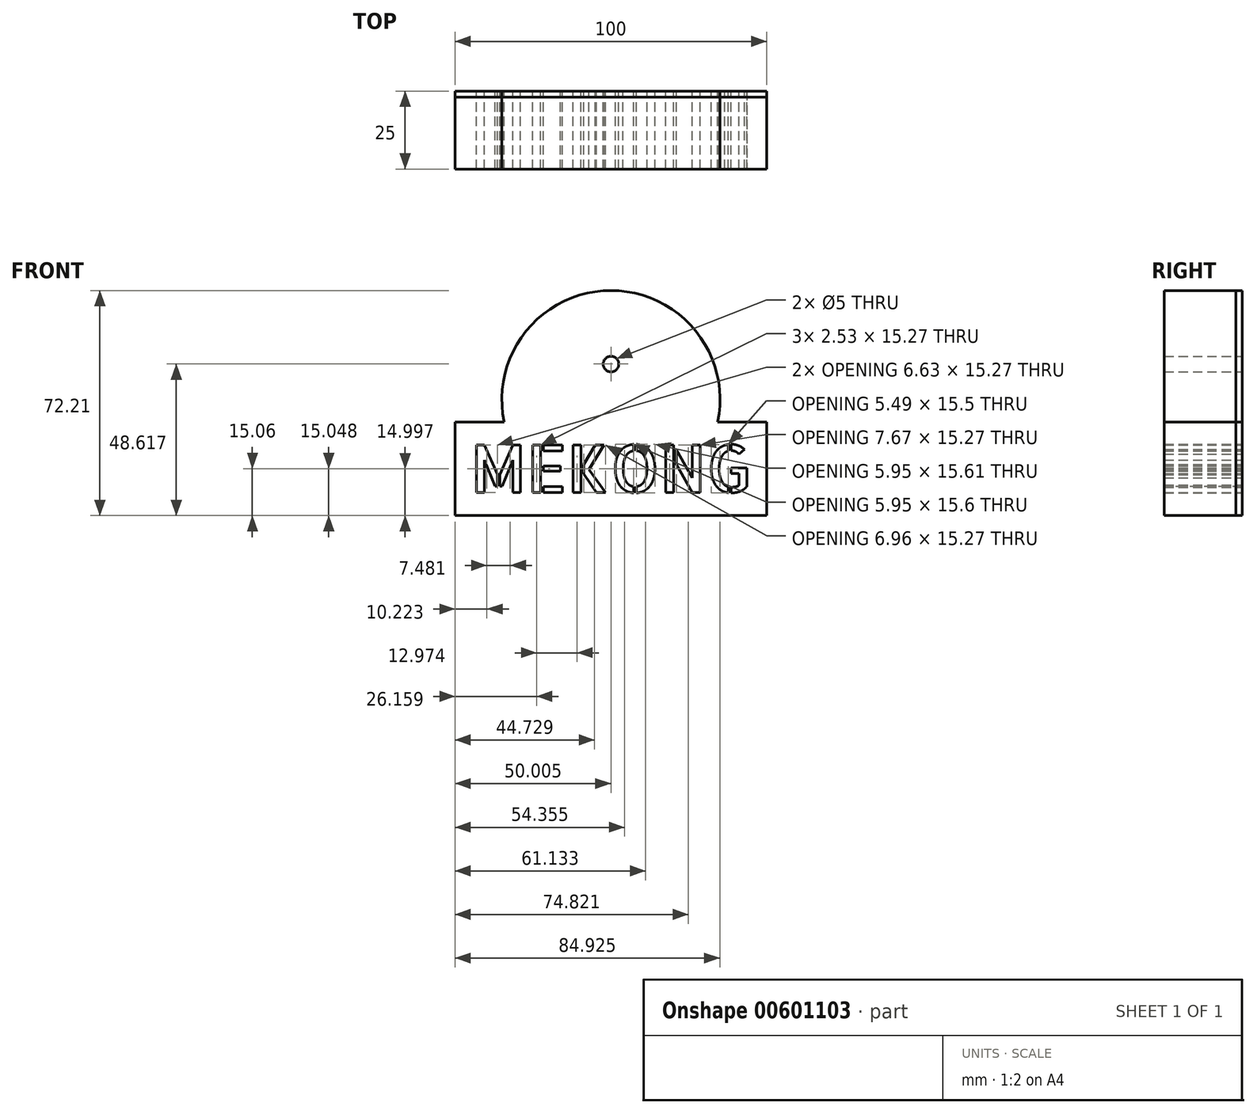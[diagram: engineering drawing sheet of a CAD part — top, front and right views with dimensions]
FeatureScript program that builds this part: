
annotation { "Feature Type Name" : "Feature", "Feature Type Description" : "" }
export const myFeature = defineFeature(function(context is Context, id is Id, definition is map)
    precondition{}
    {
        {
            var Q0;
            Q0=qCreatedBy(makeId("Front.planeOp"),FACE);
            var sketch = newSketch(context, id + "F0", { "sketchPlane" : qUnion([Q0])});
            skLineSegment(sketch, "E0.bottom", {"start": v(-209.66, -19.26) * mm, "end": v(-109.66, -19.26) * mm});
            skLineSegment(sketch, "E0.top", {"start": v(-209.66, 10.74) * mm, "end": v(-193.9, 10.74) * mm});
            skLineSegment(sketch, "E0.left", {"start": v(-209.66, -19.26) * mm, "end": v(-209.66, 10.74) * mm});
            skLineSegment(sketch, "E0.right", {"start": v(-109.66, -19.26) * mm, "end": v(-109.66, 10.74) * mm});
            skArc(sketch, "E1", {"start": v(-125.4, 10.74) * mm, "mid": v(-159.66, 52.95) * mm, "end": v(-193.9, 10.74) * mm});
            skCircle(sketch, "E2", {"center": v(-159.66, 29.36) * mm, "radius": 2.5 * mm});
            skPoint(sketch, "E3", {"position": v(-159.66, -19.26) * mm});
            skPoint(sketch, "E4", {"position": v(-109.66, -19.26) * mm});
            skPoint(sketch, "E5", {"position": v(-109.66, -4.26) * mm});
            skPoint(sketch, "E6", {"position": v(-109.66, 10.74) * mm});
            skText(sketch, "E7", { "text": "MEKONG", "fontName": "AllertaStencil-Regular.ttf"});
            skPoint(sketch, "E8", {"position": v(-159.66, -11.9) * mm});
            skPoint(sketch, "E9", {"position": v(-114.66, 3.38) * mm});
            skPoint(sketch, "E10", {"position": v(-114.66, -4.26) * mm});
            skLineSegment(sketch, "E11.trimOffspring", {"start": v(-125.4, 10.74) * mm, "end": v(-109.66, 10.74) * mm});
            const initialGuessF0  = {"E7": [-0.20466, -0.0119, 1, 0, 0.01528]};
            skSetInitialGuess(sketch, initialGuessF0);
            skSolve(sketch);
        }
        {
            var Q0;
            Q0 = qSketchRegion(id + "F0", true);
            var Q1;
            Q1=makeQuery(id+"F0.imprint","IMPRINT",FACE,{"disambiguationData":[TD([[makeQuery(id+"F0.imprint","IMPRINT",EDGE,{"derivedFrom":sQuery(id+"F0.wireOp",EDGE,"E0.bottom")}),1.0]])]});
            var Q2;
            Q2=makeQuery(id+"F0.imprint","IMPRINT",FACE,{"disambiguationData":[TD([[makeQuery(id+"F0.imprint","IMPRINT",EDGE,{"derivedFrom":sQuery(id+"F0.wireOp",EDGE,"E7.sketch_text.stroke-116")}),-1.0]])]});
            var Q3;
            Q3=makeQuery(id+"F0.imprint","IMPRINT",FACE,{"disambiguationData":[TD([[makeQuery(id+"F0.imprint","IMPRINT",EDGE,{"derivedFrom":sQuery(id+"F0.wireOp",EDGE,"E7.sketch_text.stroke-90")}),-1.0]])]});
            var Q4;
            Q4=makeQuery(id+"F0.imprint","IMPRINT",FACE,{"disambiguationData":[TD([[makeQuery(id+"F0.imprint","IMPRINT",EDGE,{"derivedFrom":sQuery(id+"F0.wireOp",EDGE,"E7.sketch_text.stroke-98")}),-1.0]])]});
            var Q5;
            Q5=makeQuery(id+"F0.imprint","IMPRINT",FACE,{"disambiguationData":[TD([[makeQuery(id+"F0.imprint","IMPRINT",EDGE,{"derivedFrom":sQuery(id+"F0.wireOp",EDGE,"E7.sketch_text.stroke-0")}),-1.0]])]});
            var Q6;
            Q6=makeQuery(id+"F0.imprint","IMPRINT",FACE,{"disambiguationData":[TD([[makeQuery(id+"F0.imprint","IMPRINT",EDGE,{"derivedFrom":sQuery(id+"F0.wireOp",EDGE,"E7.sketch_text.stroke-8")}),-1.0]])]});
            var Q7;
            Q7=makeQuery(id+"F0.imprint","IMPRINT",FACE,{"disambiguationData":[TD([[makeQuery(id+"F0.imprint","IMPRINT",EDGE,{"derivedFrom":sQuery(id+"F0.wireOp",EDGE,"E7.sketch_text.stroke-16")}),-1.0]])]});
            var Q8;
            Q8=makeQuery(id+"F0.imprint","IMPRINT",FACE,{"disambiguationData":[TD([[makeQuery(id+"F0.imprint","IMPRINT",EDGE,{"derivedFrom":sQuery(id+"F0.wireOp",EDGE,"E7.sketch_text.stroke-20")}),-1.0]])]});
            var Q9;
            Q9=makeQuery(id+"F0.imprint","IMPRINT",FACE,{"disambiguationData":[TD([[makeQuery(id+"F0.imprint","IMPRINT",EDGE,{"derivedFrom":sQuery(id+"F0.wireOp",EDGE,"E7.sketch_text.stroke-24")}),-1.0]])]});
            var Q10;
            Q10=makeQuery(id+"F0.imprint","IMPRINT",FACE,{"disambiguationData":[TD([[makeQuery(id+"F0.imprint","IMPRINT",EDGE,{"derivedFrom":sQuery(id+"F0.wireOp",EDGE,"E7.sketch_text.stroke-28")}),-1.0]])]});
            var Q11;
            Q11=makeQuery(id+"F0.imprint","IMPRINT",FACE,{"disambiguationData":[TD([[makeQuery(id+"F0.imprint","IMPRINT",EDGE,{"derivedFrom":sQuery(id+"F0.wireOp",EDGE,"E7.sketch_text.stroke-32")}),-1.0]])]});
            var Q12;
            Q12=makeQuery(id+"F0.imprint","IMPRINT",FACE,{"disambiguationData":[TD([[makeQuery(id+"F0.imprint","IMPRINT",EDGE,{"derivedFrom":sQuery(id+"F0.wireOp",EDGE,"E7.sketch_text.stroke-36")}),-1.0]])]});
            var Q13;
            Q13=makeQuery(id+"F0.imprint","IMPRINT",FACE,{"disambiguationData":[TD([[makeQuery(id+"F0.imprint","IMPRINT",EDGE,{"derivedFrom":sQuery(id+"F0.wireOp",EDGE,"E7.sketch_text.stroke-43")}),-1.0]])]});
            var Q14;
            Q14=makeQuery(id+"F0.imprint","IMPRINT",FACE,{"disambiguationData":[TD([[makeQuery(id+"F0.imprint","IMPRINT",EDGE,{"derivedFrom":sQuery(id+"F0.wireOp",EDGE,"E7.sketch_text.stroke-61")}),-1.0]])]});
            var Q15;
            Q15=makeQuery(id+"F0.imprint","IMPRINT",FACE,{"disambiguationData":[TD([[makeQuery(id+"F0.imprint","IMPRINT",EDGE,{"derivedFrom":sQuery(id+"F0.wireOp",EDGE,"E7.sketch_text.stroke-79")}),-1.0]])]});
            var Q16;
            Q16=makeQuery(id+"F0.imprint","IMPRINT",FACE,{"disambiguationData":[TD([[makeQuery(id+"F0.imprint","IMPRINT",EDGE,{"derivedFrom":sQuery(id+"F0.wireOp",EDGE,"E7.sketch_text.stroke-86")}),-1.0]])]});
            extrude(context, id + "F1", {"entities" : qUnion([Q0, Q1, Q2, Q3, Q4, Q5, Q6, Q7, Q8, Q9, Q10, Q11, Q12, Q13, Q14, Q15, Q16]), "depth" : 2 * mm, "offsetDistance" : 25 * mm});
        }
        {
            var Q0;
            Q0=makeQuery(id+"F0.imprint","IMPRINT",FACE,{"disambiguationData":[TD([[makeQuery(id+"F0.imprint","IMPRINT",EDGE,{"derivedFrom":sQuery(id+"F0.wireOp",EDGE,"E0.bottom")}),1.0]])]});
            extrude(context, id + "F2", {"entities" : qUnion([Q0]), "depth" : 25 * mm, "offsetDistance" : 25 * mm});
        }
    });
